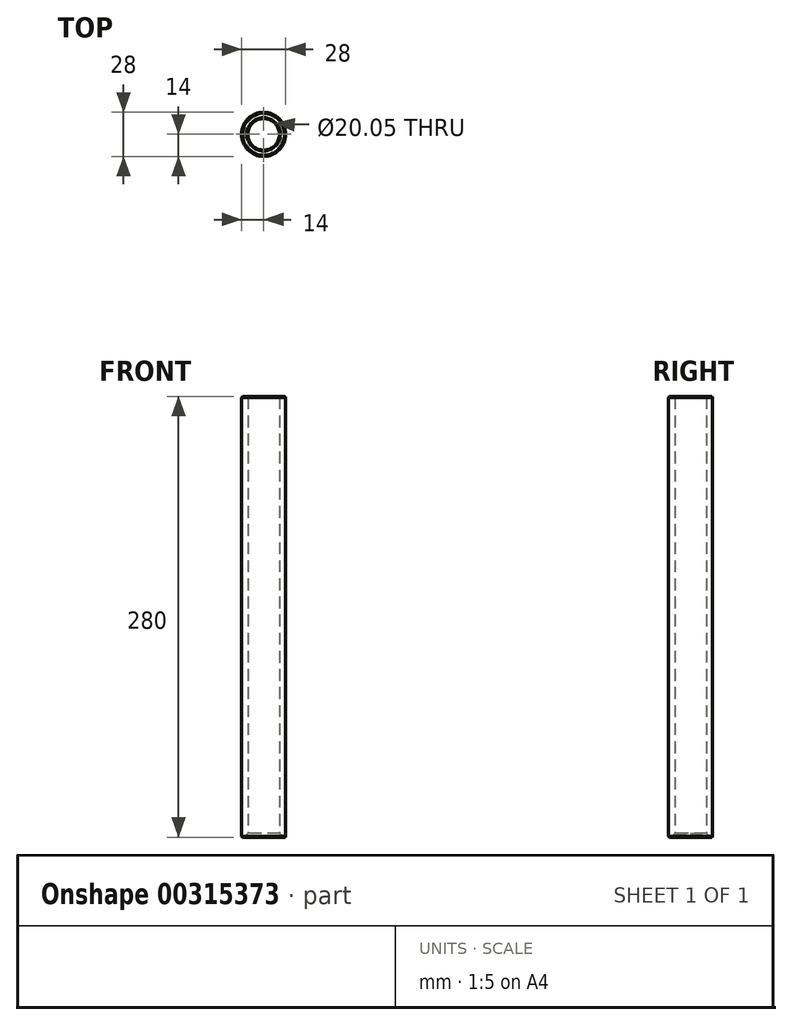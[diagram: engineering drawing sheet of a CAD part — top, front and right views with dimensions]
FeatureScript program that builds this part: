
annotation { "Feature Type Name" : "Feature", "Feature Type Description" : "" }
export const myFeature = defineFeature(function(context is Context, id is Id, definition is map)
    precondition{}
    {
        {
            var Q0;
            Q0=qCreatedBy(makeId("Top.planeOp"),FACE);
            var sketch = newSketch(context, id + "F0", { "sketchPlane" : qUnion([Q0])});
            skCircle(sketch, "E0", {"center": v(0, 0) * mm, "radius": 14 * mm});
            skCircle(sketch, "E1", {"center": v(0, 0) * mm, "radius": 10.03 * mm});
            skSolve(sketch);
        }
        {
            var Q0;
            Q0 = qSketchRegion(id + "F0", true);
            extrude(context, id + "F1", {"entities" : qUnion([Q0]), "depth" : 280 * mm});
        }
        {
            var Q0;
            Q0=makeQuery(id+"F1.opExtrude","CAP_EDGE",EDGE,{"disambiguationData":[OSD([sQuery(id+"F0.wireOp",EDGE,"E1")])],"isStart":false});
            var Q1;
            Q1=makeQuery(id+"F1.opExtrude","CAP_EDGE",EDGE,{"disambiguationData":[OSD([sQuery(id+"F0.wireOp",EDGE,"E0")])],"isStart":false});
            var Q2;
            Q2=makeQuery(id+"F1.opExtrude","CAP_EDGE",EDGE,{"disambiguationData":[OSD([sQuery(id+"F0.wireOp",EDGE,"E0")])],"isStart":true});
            chamfer(context, id + "F2", {"entities" : qUnion([Q0, Q1, Q2]), "width" : 0.6 * mm, "tangentPropagation" : true});
        }
        {
            var Q0;
            Q0=makeQuery(id+"F1.opExtrude","CAP_EDGE",EDGE,{"disambiguationData":[OSD([sQuery(id+"F0.wireOp",EDGE,"E1")])],"isStart":true});
            chamfer(context, id + "F3", {"entities" : qUnion([Q0]), "width" : 2.5 * mm, "tangentPropagation" : true});
        }
    });
